# Revit family: xShower_Head-GROHE-New_Tempesta_Cosmopolitan_100-26043_Series
name_source: partatom
category: Plumbing Fixtures
revit_build: Autodesk Revit 2018 (Build: 20170223_1515(x64)
units: mm (PartAtom-declared; Revit-internal decimal feet)

## family parameters
Always vertical = No
Cut with Voids When Loaded = No
OmniClass Number = 23.45.05.14.17
OmniClass Title = Showers
Part Type = Normal
Room Calculation Point = No
Round Connector Dimension = Use Diameter
Shared = Yes
Work Plane-Based = Yes

## types (5) — shared parameters
CW Connection = Yes
CWFU = 3
Default Elevation = 0"
Description = Tempesta Cosmopolitan 100 Shower Head
Diameter = 3 15/16"
Flow Rate = 1.75 gpm (6.6 l/min)
HW Connection = Yes
HWFU = 3
Height = 3 5/16"
IAPMO Compliance = ASME A112.18.1/CSA B125.1
Manufacturer = GROHE
Min. Working Pressure = 15 psi (1.0 bar)
Price = Prices may vary. Please consult Manufacturer Representative for most up-to-date price list.
Product Documentation Link = https://americanstandard.box.com
Product Page URL = https://www.grohe.us
Revised Date = 05/27/2021
Tempered Water Connection Diameter = 1/2"
Tempered Water Connection Radius = 1/4"
URL = https://www.grohe.us
Vent Connection = No
Warranty Documentation Link = https://cdn.cloud.grohe.com
Waste Connection = No
cUPC Compliant = Yes
zero-valued in all types: WFU

## per-type parameters (varying)
| type | Assembly Code | Finish | Material |
| 26043001 | D2010710 | Metal-Grohe-001-StarLight Chrome | Metal-Grohe-001-StarLight Chrome |
| 26043EN1 | D2010700 | Metal-Grohe-EN1-Brushed Nickel Infinity Finish | Metal-Grohe-EN1-Brushed Nickel Infinity Finish |
| 26043A01 | D2010710 | Metal-Grohe-A01-Hard Graphite | Metal-Grohe-A01-Hard Graphite |
| 26043BE1 | D2010710 | Metal-Grohe-BE1-Polished Nickel Infinity Finish | Metal-Grohe-BE1-Polished Nickel Infinity Finish |
| 26043GN1 | D2010710 | Metal-Grohe-GN1-Brushed Cool Sunrise | Metal-Grohe-GN1-Brushed Cool Sunrise |

note: column(s) folded — value = type name in every type: Model

## geometry (parser evidence)
native form markers: Sweep x1
no freeform markers — native parametric forms only
